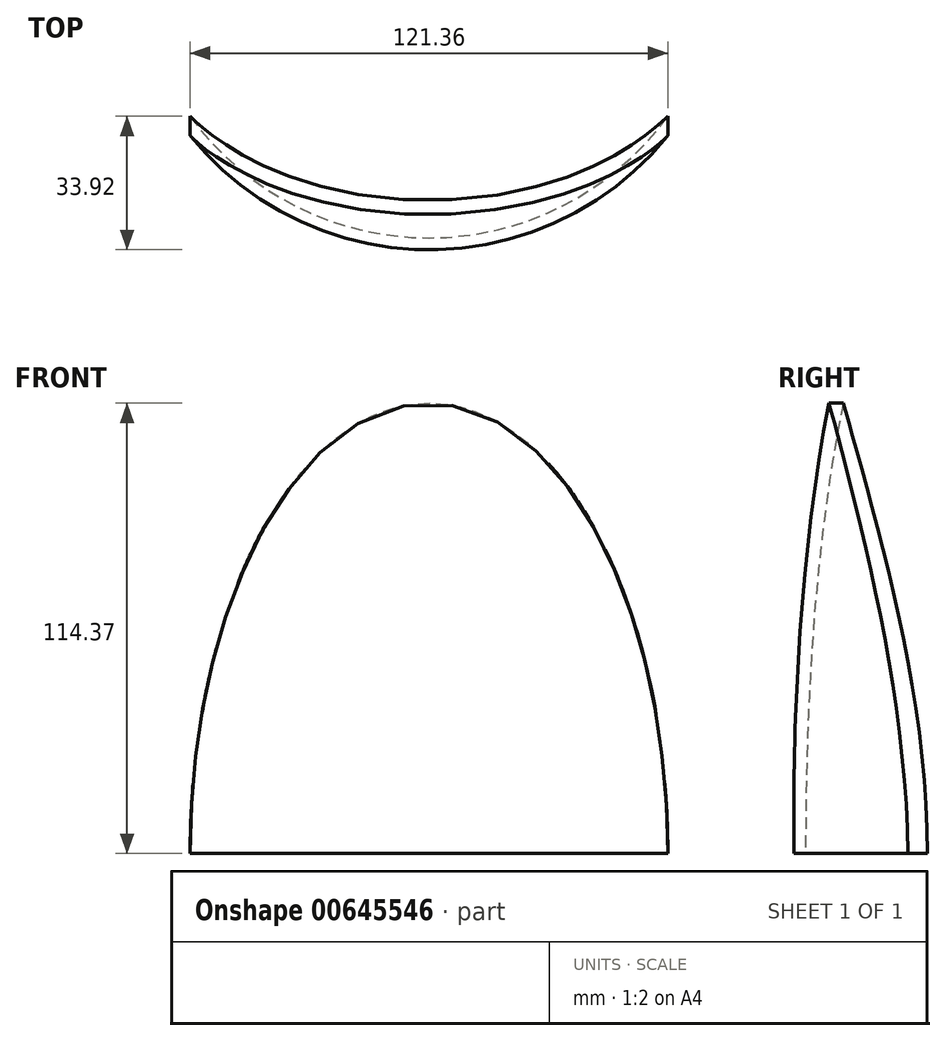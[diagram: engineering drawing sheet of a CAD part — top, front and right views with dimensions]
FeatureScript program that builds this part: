
annotation { "Feature Type Name" : "Feature", "Feature Type Description" : "" }
export const myFeature = defineFeature(function(context is Context, id is Id, definition is map)
    precondition{}
    {
        {
            var Q0;
            Q0=qCreatedBy(makeId("Front.planeOp"),FACE);
            var sketch = newSketch(context, id + "F0", { "sketchPlane" : qUnion([Q0])});
            skLineSegment(sketch, "E0", {"start": v(0, 0) * mm, "end": v(75, 0) * mm, "construction": true});
            skLineSegment(sketch, "E1", {"start": v(0, 0) * mm, "end": v(0, 200) * mm, "construction": true});
            skFitSpline(sketch, "E2", {"points": [v(0, 200) * mm, v(75, 0) * mm], "startDerivative": vector(195.84, 0) * mm, "endDerivative": vector(0, -233.52) * mm});
            skLineSegment(sketch, "E3", {"start": v(0, 200) * mm, "end": v(-73.01, 200) * mm, "construction": true});
            skLineSegment(sketch, "E4", {"start": v(75, 0) * mm, "end": v(75, -62.44) * mm, "construction": true});
            skFitSpline(sketch, "E5.0", {"points": [v(0, 203) * mm, v(4.31, 203) * mm, v(12.54, 201.99) * mm, v(23.6, 197.66) * mm, v(33.34, 190.84) * mm, v(41.8, 181.87) * mm, v(49.09, 171.07) * mm, v(57.4, 154.55) * mm, v(65.4, 130.54) * mm, v(71.87, 98.22) * mm, v(75.78, 64.3) * mm, v(77.7, 30.68) * mm, v(78, 9.76) * mm, v(78, 0) * mm]});
            skLineSegment(sketch, "E6", {"start": v(75, 0) * mm, "end": v(78, 0) * mm});
            skLineSegment(sketch, "E7", {"start": v(0, 203) * mm, "end": v(0, 200) * mm});
            skSolve(sketch);
        }
        {
            var Q0;
            Q0 = qSketchRegion(id + "F0", true);
            var Q1;
            Q1=sQuery(id+"F0.wireOp",EDGE,"E1");
            revolve(context, id + "F1", {"entities" : qUnion([Q0]), "axis" : qUnion([Q1]), "revolveType" : RevolveType.ONE_DIRECTION, "oppositeDirection" : true, "angle" : 180 * degree});
        }
        {
            var Q0;
            Q0=qCreatedBy(makeId("Front.planeOp"),FACE);
            var sketch = newSketch(context, id + "F2", { "sketchPlane" : qUnion([Q0])});
            skEllipticalArc(sketch, "E8", {});
            skLineSegment(sketch, "E9.bottom", {"start": v(-100.41, 216.58) * mm, "end": v(117.88, 216.58) * mm});
            skLineSegment(sketch, "E9.top", {"start": v(-100.41, -10.87) * mm, "end": v(-60.4, -10.87) * mm});
            skLineSegment(sketch, "E9.left", {"start": v(-100.41, 216.58) * mm, "end": v(-100.41, -10.87) * mm});
            skLineSegment(sketch, "E9.right", {"start": v(117.88, 216.58) * mm, "end": v(117.88, -10.87) * mm});
            skLineSegment(sketch, "E10.trimOffspring", {"start": v(60.4, -10.87) * mm, "end": v(117.88, -10.87) * mm});
            const initialGuessF2  = {"E8": [0, 0, 0, 1, 0.11436499523005736, 0.06067914517220728, 4.617241717347879, 1.6659435898317072]};
            skSetInitialGuess(sketch, initialGuessF2);
            skSolve(sketch);
        }
        {
            var Q0;
            Q0 = qSketchRegion(id + "F2", true);
            extrude(context, id + "F3", {"entities" : qUnion([Q0]), "operationType" : NewBodyOperationType.REMOVE, "depth" : 94 * mm, "offsetDistance" : 25 * mm});
        }
        {
            var Q0;
            Q0=qCreatedBy(makeId("Right.planeOp"),FACE);
            var sketch = newSketch(context, id + "F4", { "sketchPlane" : qUnion([Q0])});
            skFitSpline(sketch, "E11", {"points": [v(-59.91, 136.48) * mm, v(-33.87, 56.53) * mm, v(-24.64, 0) * mm], "startDerivative": vector(54.98, -151.66) * mm, "endDerivative": vector(3.6, -133.86) * mm});
            skLineSegment(sketch, "E12", {"start": v(-59.91, 136.48) * mm, "end": v(-24.64, 129.96) * mm});
            skLineSegment(sketch, "E13", {"start": v(-24.64, 129.96) * mm, "end": v(-12.16, -9.85) * mm});
            skLineSegment(sketch, "E14", {"start": v(-12.16, -9.85) * mm, "end": v(-19.4, -8.4) * mm});
            skLineSegment(sketch, "E15", {"start": v(-19.4, -8.4) * mm, "end": v(-24.64, 0) * mm});
            skSolve(sketch);
        }
        {
            var Q0;
            Q0 = qSketchRegion(id + "F4", true);
            extrude(context, id + "F5", {"entities" : qUnion([Q0]), "operationType" : NewBodyOperationType.REMOVE, "endBound" : BoundingType.SYMMETRIC, "oppositeDirection" : true, "depth" : 203 * mm, "offsetDistance" : 25 * mm});
        }
    });
